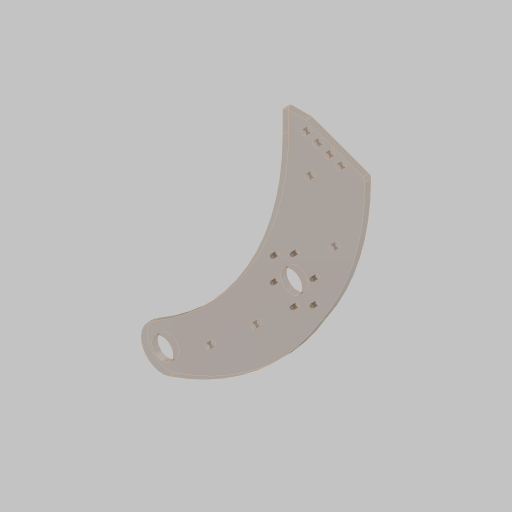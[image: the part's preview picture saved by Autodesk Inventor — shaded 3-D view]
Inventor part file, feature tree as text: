
AUTODESK INVENTOR PART (.ipt)
format: ipt  version: 2023.5 (Build 275446000, 446)  size: 257,536 bytes
history: native  units: in
note: dims shown in document units (in); Inventor stores cm internally (conversion verified against a paired STEP export)
features: sketch x5, hole x4, projected_geometry x3, extrude x2, fillet x2
ambient origin geometry x8: Origin, YZ Plane, XZ Plane, XY Plane, X Axis, Y Axis, Z Axis, Center Point
bodies: Solid1 (feature_tree)
feature tree (16):
  sketch  "Sketch1"  dims[d0=1.0in d1=5.0in]
  extrude  "Extrusion1"  Depth=5.0in
  hole  "Hole1"  [1 undecoded]
  hole  "Hole2"  [1 undecoded]
  fillet  "Fillet1"  Radius=0.5in
  hole  "Hole3"  [1 undecoded]
  hole  "Hole4"  [1 undecoded]
  extrude  "Extrusion2"  Depth=0.25in
  fillet  "Fillet2"  Radius=11.5in
  sketch  "Sketch5"  dims[d8=1.875in d9=0.875in]
  sketch  "Sketch3"  dims[d2=8.75in d3=5.75in]
  projected_geometry  "Projected Loop1"
  sketch  "Sketch4"  dims[d4=1.0in d5=5.0in d7=0.5in]
  projected_geometry  "Projected Loop2"
  sketch  "Sketch6"  dims[d10=1.9685in d12=0.5in d13=0.3937in d15=1.0in d17=0.5in d18=0.375in d19=11.5in d20=0.25in d21=0.0in d22=0.201in d23=0.38in d24=0.385in d25=0.25in d26=0.5635in d27=1.0in d28=0.8108in d29=0.875in d30=0.75in d31=0.507in d32=0.25in d33=0.5635in d34=1.0in d35=0.8108in d37=5.75in d38=2.5in d39=0.1374in d40=1.5748in d42=0.5in d43=0.3937in d45=1.0in d47=0.5in d48=0.125in d49=1.875in d50=2.3622in d52=360.0deg d54=0.156in d55=0.38in d56=0.385in d57=0.25in d58=0.5635in d59=1.0in d60=0.8108in d62=0.25in d63=0.25in d64=0.25in d65=0.25in d66=0.25in d67=0.25in d68=0.875in d69=0.875in d70=0.5in d71=0.125in d72=0.0in d73=0.13in d74=13.8531in d75=5.0044in d76=2.0in d77=2.0in d78=1.0in d79=1.0in d84=0.201in d85=0.75in d86=0.385in d87=0.25in d88=0.5635in d89=1.0in d90=0.8108in d91=10.25in d92=2.5in d93=1.0in]
  projected_geometry  "Projected Loop3"
note: 4 required parameter values undecoded (feature->parameter linkage not recoverable at this tier; creation-order binding heuristic only, values carry confidence <= 0.55)
